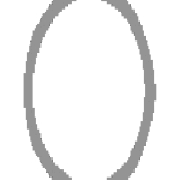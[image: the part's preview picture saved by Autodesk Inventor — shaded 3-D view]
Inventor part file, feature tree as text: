
AUTODESK INVENTOR PART (.ipt)
format: ipt  version: 2021 (Build 250183000, 183)  size: 109,568 bytes
history: native  units: in
note: dims shown in document units (in); Inventor stores cm internally (conversion verified against a paired STEP export)
features: other x4, sketch x3, plane x1
ambient origin geometry x8: Origin, YZ Plane, XZ Plane, XY Plane, X Axis, Y Axis, Z Axis, Center Point
bodies: Solid1 (feature_tree), Body (feature_tree)
feature tree (8):
  other  "Driven Length"
  other  "Frame Generator"
  other  "Start Plane"
  other  "End Plane"
  sketch  "Sketch"  dims[d2=29.4in d4=-0.0in d5=29.4in d6=0.12in d7=0.0in d8=90.0deg d9=29.4in]
  sketch  "Sketch2"  dims[d0=1.0in]
  plane  "Work Plane3"
  sketch  "Sketch3"  dims[d1=0.065in]
